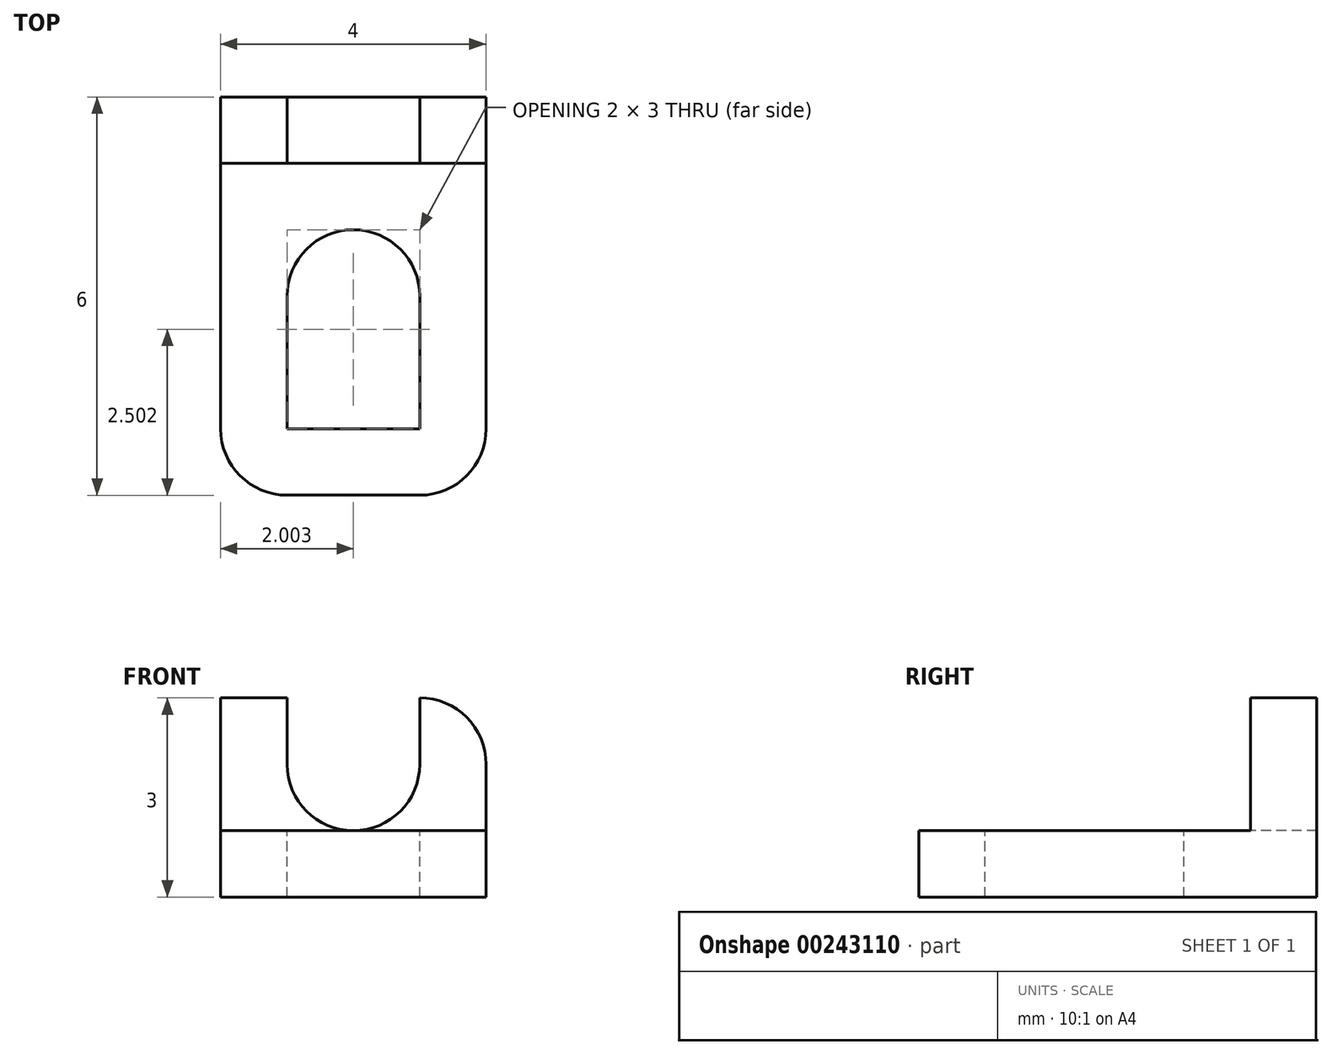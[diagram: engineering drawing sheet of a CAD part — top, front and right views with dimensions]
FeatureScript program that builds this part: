
annotation { "Feature Type Name" : "Feature", "Feature Type Description" : "" }
export const myFeature = defineFeature(function(context is Context, id is Id, definition is map)
    precondition{}
    {
        {
            var Q0;
            Q0=qCreatedBy(makeId("Top.planeOp"),FACE);
            var sketch = newSketch(context, id + "F0", { "sketchPlane" : qUnion([Q0])});
            skLineSegment(sketch, "E0.bottom", {"start": v(13.11, -0.95) * mm, "end": v(9.11, -0.95) * mm});
            skLineSegment(sketch, "E0.top", {"start": v(13.11, 5.05) * mm, "end": v(9.11, 5.05) * mm});
            skLineSegment(sketch, "E0.left", {"start": v(13.11, -0.95) * mm, "end": v(13.11, 5.05) * mm});
            skLineSegment(sketch, "E0.right", {"start": v(9.11, -0.95) * mm, "end": v(9.11, 5.05) * mm});
            skSolve(sketch);
        }
        {
            var Q0;
            Q0 = qSketchRegion(id + "F0", true);
            extrude(context, id + "F1", {"entities" : qUnion([Q0]), "depth" : 1 * mm});
        }
        {
            var Q0;
            Q0=makeQuery(id+"F1.opExtrude","CAP_FACE",FACE,{"disambiguationData":[OSD([sQuery(id+"F0.wireOp",EDGE,"E0.bottom"),sQuery(id+"F0.wireOp",EDGE,"E0.top"),sQuery(id+"F0.wireOp",EDGE,"E0.left"),sQuery(id+"F0.wireOp",EDGE,"E0.right")])],"isStart":false});
            var sketch = newSketch(context, id + "F2", { "sketchPlane" : qUnion([Q0])});
            skLineSegment(sketch, "E1", {"start": v(10.11, 0.05) * mm, "end": v(12.11, 0.05) * mm});
            skLineSegment(sketch, "E2", {"start": v(12.11, 0.05) * mm, "end": v(12.11, 2.05) * mm});
            skLineSegment(sketch, "E3", {"start": v(12.11, 2.05) * mm, "end": v(10.11, 2.05) * mm});
            skLineSegment(sketch, "E4", {"start": v(10.11, 2.05) * mm, "end": v(10.11, 0.05) * mm});
            skCircle(sketch, "E5", {"center": v(11.11, 2.05) * mm, "radius": 1 * mm});
            skSolve(sketch);
        }
        {
            var Q0;
            Q0 = qSketchRegion(id + "F2", true);
            extrude(context, id + "F3", {"entities" : qUnion([Q0]), "operationType" : NewBodyOperationType.REMOVE, "oppositeDirection" : true, "depth" : 25 * mm});
        }
        {
            var Q0;
            Q0=makeQuery(id+"F1.opExtrude","CAP_FACE",FACE,{"disambiguationData":[OSD([sQuery(id+"F0.wireOp",EDGE,"E0.bottom"),sQuery(id+"F0.wireOp",EDGE,"E0.top"),sQuery(id+"F0.wireOp",EDGE,"E0.left"),sQuery(id+"F0.wireOp",EDGE,"E0.right")])],"isStart":false});
            var sketch = newSketch(context, id + "F4", { "sketchPlane" : qUnion([Q0])});
            skLineSegment(sketch, "E6", {"start": v(9.11, 5.05) * mm, "end": v(9.11, 4.05) * mm});
            skLineSegment(sketch, "E7", {"start": v(9.11, 4.05) * mm, "end": v(13.11, 4.05) * mm});
            skLineSegment(sketch, "E8", {"start": v(13.11, 4.05) * mm, "end": v(13.11, 5.05) * mm});
            skLineSegment(sketch, "E9", {"start": v(13.11, 5.05) * mm, "end": v(9.11, 5.05) * mm});
            skSolve(sketch);
        }
        {
            var Q0;
            Q0 = qSketchRegion(id + "F4", true);
            extrude(context, id + "F5", {"entities" : qUnion([Q0]), "operationType" : NewBodyOperationType.ADD, "depth" : 2 * mm});
        }
        {
            var Q0;
            Q0=makeQuery(id+"F5.opExtrude","CAP_EDGE",EDGE,{"disambiguationData":[OSD([sQuery(id+"F4.wireOp",EDGE,"E8")])],"isStart":false});
            var Q1;
            Q1=makeQuery(id+"F1.opExtrude","SWEPT_EDGE",EDGE,{"disambiguationData":[OSD([sQuery(id+"F0.wireOp",EDGE,"E0.bottom"),sQuery(id+"F0.wireOp",EDGE,"E0.left")])]});
            var Q2;
            Q2=makeQuery(id+"F1.opExtrude","SWEPT_EDGE",EDGE,{"disambiguationData":[OSD([sQuery(id+"F0.wireOp",EDGE,"E0.bottom"),sQuery(id+"F0.wireOp",EDGE,"E0.right")])]});
            fillet(context, id + "F6", {"entities" : qUnion([Q0, Q1, Q2]), "radius" : 1 * mm, "tangentPropagation" : true, "allowEdgeOverflow" : false});
        }
        {
            var Q0;
            Q0=makeQuery(id+"F5.opExtrude","SWEPT_FACE",FACE,{"disambiguationData":[OSD([sQuery(id+"F4.wireOp",EDGE,"E7")])]});
            var sketch = newSketch(context, id + "F7", { "sketchPlane" : qUnion([Q0])});
            skLineSegment(sketch, "E10", {"start": v(10.11, 3) * mm, "end": v(10.11, 2) * mm});
            skLineSegment(sketch, "E11", {"start": v(12.11, 2) * mm, "end": v(12.11, 3) * mm});
            skCircle(sketch, "E12", {"center": v(11.11, 2) * mm, "radius": 1 * mm});
            skLineSegment(sketch, "E13", {"start": v(10.11, 3) * mm, "end": v(12.11, 3) * mm});
            skSolve(sketch);
        }
        {
            var Q0;
            Q0 = qSketchRegion(id + "F7", true);
            extrude(context, id + "F8", {"entities" : qUnion([Q0]), "operationType" : NewBodyOperationType.REMOVE, "oppositeDirection" : true, "depth" : 1 * mm});
        }
    });
